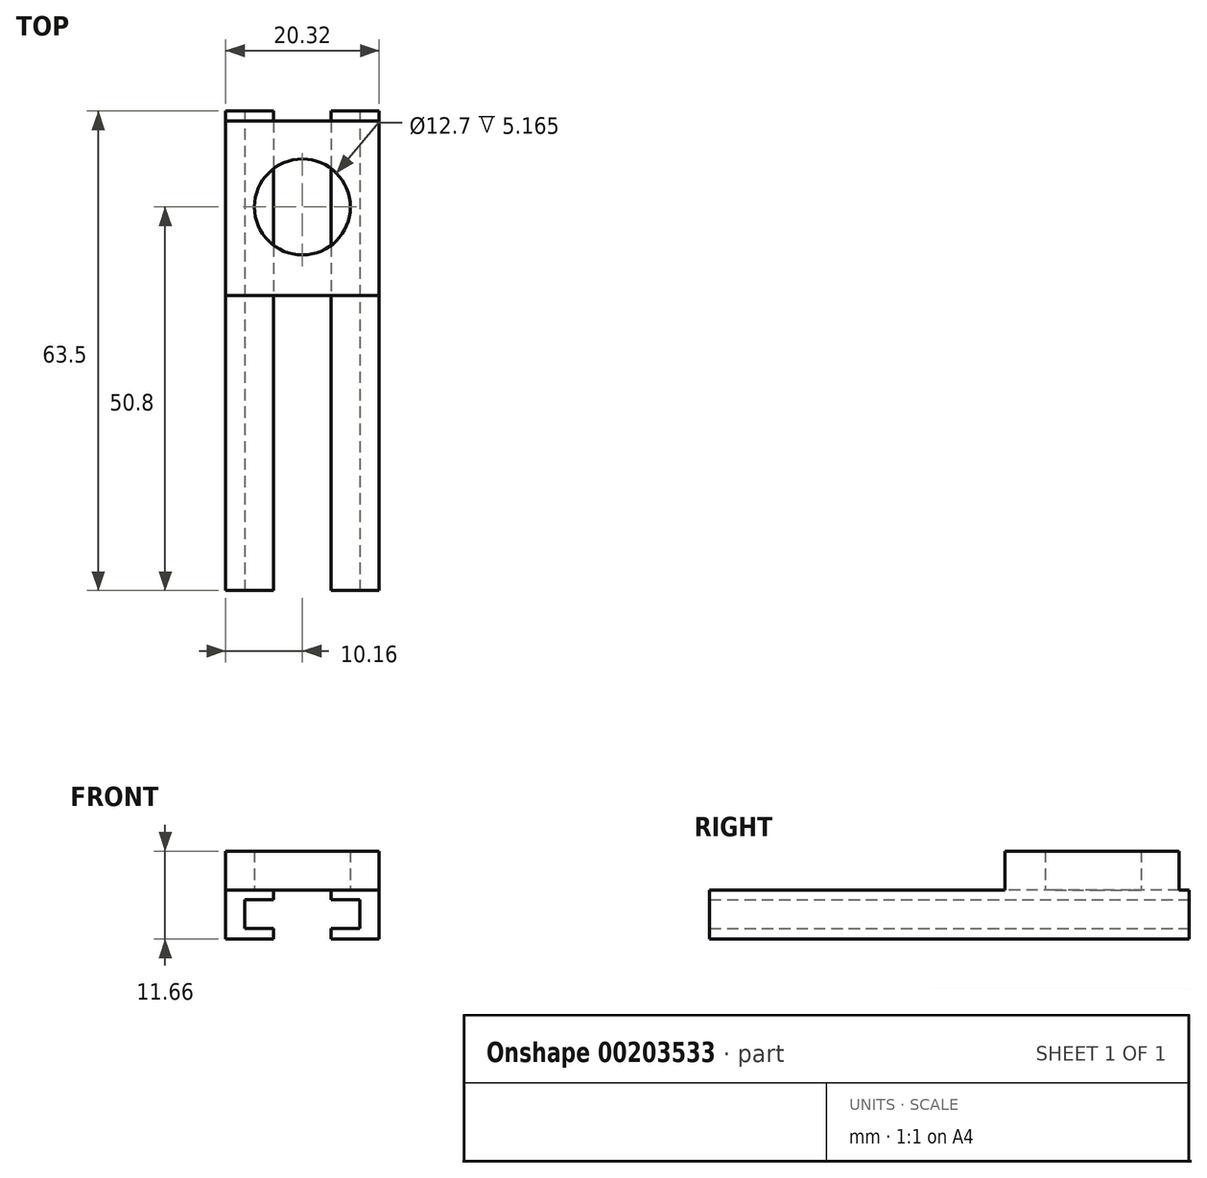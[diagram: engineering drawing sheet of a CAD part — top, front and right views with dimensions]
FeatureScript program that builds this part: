
annotation { "Feature Type Name" : "Feature", "Feature Type Description" : "" }
export const myFeature = defineFeature(function(context is Context, id is Id, definition is map)
    precondition{}
    {
        {
            var Q0;
            Q0=qCreatedBy(makeId("Right.planeOp"),FACE);
            var sketch = newSketch(context, id + "F0", { "sketchPlane" : qUnion([Q0])});
            skLineSegment(sketch, "E0.bottom", {"start": v(11.36, 5.16) * mm, "end": v(-11.73, 5.16) * mm});
            skLineSegment(sketch, "E0.top", {"start": v(11.36, 0) * mm, "end": v(-11.73, 0) * mm});
            skLineSegment(sketch, "E0.left", {"start": v(11.36, 5.16) * mm, "end": v(11.36, 0) * mm});
            skLineSegment(sketch, "E0.right", {"start": v(-11.73, 5.16) * mm, "end": v(-11.73, 0) * mm});
            skSolve(sketch);
        }
        {
            var Q0;
            Q0=makeQuery(id+"F0.imprint","IMPRINT",FACE,{"disambiguationData":[TD([[makeQuery(id+"F0.imprint","IMPRINT",EDGE,{"derivedFrom":sQuery(id+"F0.wireOp",EDGE,"E0.bottom")}),1.0]])]});
            extrude(context, id + "F1", {"entities" : qUnion([Q0]), "depth" : 10.16 * mm, "hasSecondDirection" : true, "secondDirectionOppositeDirection" : true, "secondDirectionDepth" : 10.16 * mm});
        }
        {
            var Q0;
            Q0=qCreatedBy(makeId("Top.planeOp"),FACE);
            var sketch = newSketch(context, id + "F2", { "sketchPlane" : qUnion([Q0])});
            skCircle(sketch, "E1", {"center": v(0, 0) * mm, "radius": 5.26 * mm});
            skSolve(sketch);
        }
        {
            var Q0;
            Q0=sQuery(id+"F2.wireOp",VERTEX,"E1.center");
            var Q1;
            Q1=makeQuery(id+"F1.opExtrude","SWEPT_BODY",BODY,{"disambiguationData":[OSD([sQuery(id+"F0.wireOp",EDGE,"E0.bottom"),sQuery(id+"F0.wireOp",EDGE,"E0.top"),sQuery(id+"F0.wireOp",EDGE,"E0.left"),sQuery(id+"F0.wireOp",EDGE,"E0.right")])]});
            hole(context, id + "F3", {"style" : HoleStyle.SIMPLE, "endStyle" : HoleEndStyle.THROUGH, "oppositeDirection" : true, "holeDiameter" : 12.7 * mm, "locations" : qUnion([Q0]), "scope" : qUnion([Q1]), "isTappedThrough" : true});
        }
        {
            var Q0;
            Q0=qCreatedBy(makeId("Front.planeOp"),FACE);
            var sketch = newSketch(context, id + "F4", { "sketchPlane" : qUnion([Q0])});
            skLineSegment(sketch, "E2", {"start": v(-3.81, 0) * mm, "end": v(-3.81, -6.5) * mm});
            skLineSegment(sketch, "E3", {"start": v(3.81, 0) * mm, "end": v(3.81, -6.48) * mm});
            skSolve(sketch);
        }
        {
            var Q0;
            Q0=sQuery(id+"F4.wireOp",EDGE,"E2");
            extrude(context, id + "F5", {"bodyType" : ToolBodyType.SURFACE, "surfaceEntities" : qUnion([Q0]), "depth" : 50.8 * mm, "hasSecondDirection" : true, "secondDirectionOppositeDirection" : true, "secondDirectionDepth" : 12.7 * mm});
        }
        {
            var Q0;
            Q0=makeQuery(id+"F5.opExtrude","SWEPT_FACE",FACE,{"disambiguationData":[OSD([sQuery(id+"F4.wireOp",EDGE,"E2")])]});
            extrude(context, id + "F6", {"entities" : qUnion([Q0]), "operationType" : NewBodyOperationType.ADD, "depth" : 6.35 * mm});
        }
        {
            var Q0;
            Q0=sQuery(id+"F4.wireOp",EDGE,"E3");
            extrude(context, id + "F7", {"bodyType" : ToolBodyType.SURFACE, "surfaceEntities" : qUnion([Q0]), "depth" : 50.8 * mm, "hasSecondDirection" : true, "secondDirectionOppositeDirection" : true, "secondDirectionDepth" : 12.7 * mm});
        }
        {
            var Q0;
            Q0=makeQuery(id+"F7.opExtrude","SWEPT_FACE",FACE,{"disambiguationData":[OSD([sQuery(id+"F4.wireOp",EDGE,"E3")])]});
            extrude(context, id + "F8", {"entities" : qUnion([Q0]), "operationType" : NewBodyOperationType.ADD, "oppositeDirection" : true, "depth" : 6.35 * mm});
        }
        {
            var Q0;
            Q0=qCreatedBy(makeId("Front.planeOp"),FACE);
            var sketch = newSketch(context, id + "F9", { "sketchPlane" : qUnion([Q0])});
            skLineSegment(sketch, "E4.bottom", {"start": v(7.62, -1.27) * mm, "end": v(-7.62, -1.27) * mm});
            skLineSegment(sketch, "E4.top", {"start": v(7.62, -5.08) * mm, "end": v(-7.62, -5.08) * mm});
            skLineSegment(sketch, "E4.left", {"start": v(7.62, -1.27) * mm, "end": v(7.62, -5.08) * mm});
            skLineSegment(sketch, "E4.right", {"start": v(-7.62, -1.27) * mm, "end": v(-7.62, -5.08) * mm});
            skSolve(sketch);
        }
        {
            var Q0;
            Q0 = qSketchRegion(id + "F9", true);
            extrude(context, id + "F10", {"entities" : qUnion([Q0]), "operationType" : NewBodyOperationType.REMOVE, "oppositeDirection" : true, "depth" : 12.7 * mm, "hasSecondDirection" : true, "secondDirectionOppositeDirection" : false, "secondDirectionDepth" : 50.8 * mm});
        }
    });
